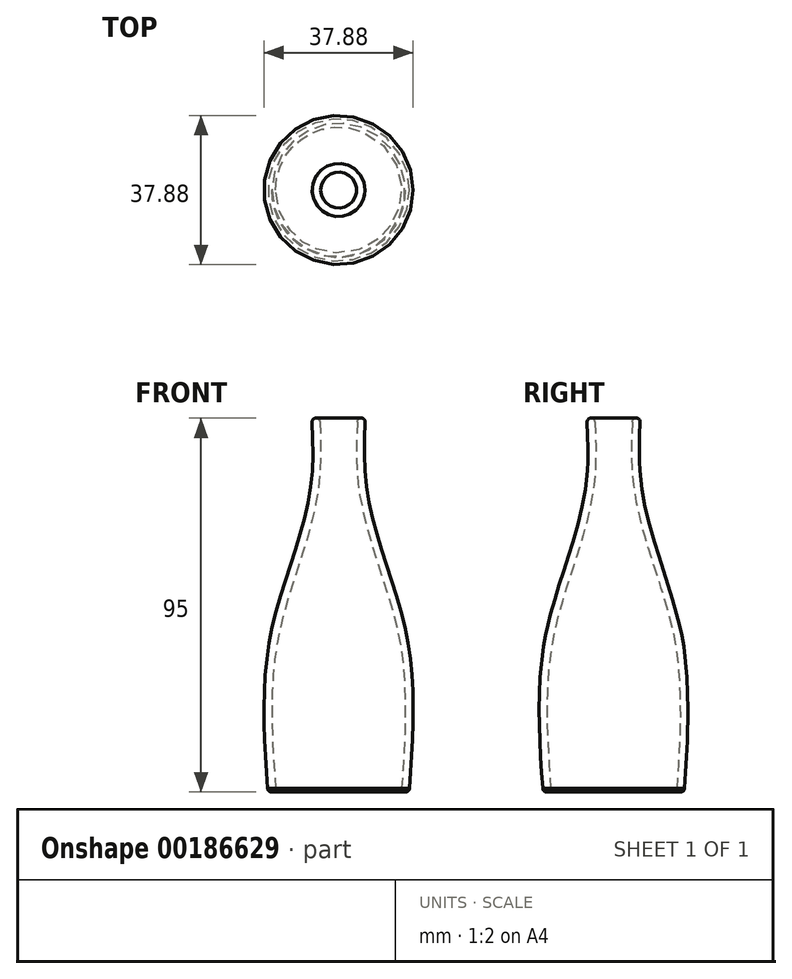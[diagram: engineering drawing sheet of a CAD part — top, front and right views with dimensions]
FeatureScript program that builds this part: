
annotation { "Feature Type Name" : "Feature", "Feature Type Description" : "" }
export const myFeature = defineFeature(function(context is Context, id is Id, definition is map)
    precondition{}
    {
        {
            var Q0;
            Q0=qCreatedBy(makeId("Top.planeOp"),FACE);
            var sketch = newSketch(context, id + "F0", { "sketchPlane" : qUnion([Q0])});
            skCircle(sketch, "E0", {"center": v(0, 0) * mm, "radius": 17.95 * mm});
            skPoint(sketch, "E1", {"position": v(0, 17.95) * mm});
            skPoint(sketch, "E2.1.0", {"position": v(-17.95, 0) * mm});
            skPoint(sketch, "E2.2.0", {"position": v(0, -17.95) * mm});
            skPoint(sketch, "E2.3.0", {"position": v(17.95, 0) * mm});
            skSolve(sketch);
        }
        {
            var Q0;
            Q0=qCreatedBy(makeId("Top.planeOp"),FACE);
            cPlane(context, id + "F1", {"entities" : qUnion([Q0]), "cplaneType" : CPlaneType.OFFSET, "offset" : 40 * mm, "width" : 150 * mm, "height" : 150 * mm});
        }
        {
            var Q0;
            Q0=qCreatedBy(id+"F1.planeOp",FACE);
            var sketch = newSketch(context, id + "F2", { "sketchPlane" : qUnion([Q0])});
            skCircle(sketch, "E3", {"center": v(0, 0) * mm, "radius": 17.25 * mm});
            skPoint(sketch, "E4", {"position": v(0, 17.25) * mm});
            skPoint(sketch, "E5.1.0", {"position": v(-17.25, 0) * mm});
            skPoint(sketch, "E5.2.0", {"position": v(0, -17.25) * mm});
            skPoint(sketch, "E5.3.0", {"position": v(17.25, 0) * mm});
            skSolve(sketch);
        }
        {
            var Q0;
            Q0=qCreatedBy(id+"F1.planeOp",FACE);
            cPlane(context, id + "F3", {"entities" : qUnion([Q0]), "cplaneType" : CPlaneType.OFFSET, "offset" : 40 * mm, "width" : 150 * mm, "height" : 150 * mm});
        }
        {
            var Q0;
            Q0=qCreatedBy(id+"F3.planeOp",FACE);
            var sketch = newSketch(context, id + "F4", { "sketchPlane" : qUnion([Q0])});
            skCircle(sketch, "E6", {"center": v(0, 0) * mm, "radius": 6.8 * mm});
            skSolve(sketch);
        }
        {
            var Q0;
            Q0=qCreatedBy(id+"F3.planeOp",FACE);
            cPlane(context, id + "F5", {"entities" : qUnion([Q0]), "cplaneType" : CPlaneType.OFFSET, "offset" : 15 * mm, "width" : 150 * mm, "height" : 150 * mm});
        }
        {
            var Q0;
            Q0=qCreatedBy(id+"F5.planeOp",FACE);
            var sketch = newSketch(context, id + "F6", { "sketchPlane" : qUnion([Q0])});
            skCircle(sketch, "E7", {"center": v(0, 0) * mm, "radius": 6.8 * mm});
            skSolve(sketch);
        }
        {
            var Q0;
            Q0=makeQuery(id+"F6.imprint","IMPRINT",FACE,{"disambiguationData":[TD([[makeQuery(id+"F6.imprint","IMPRINT",EDGE,{"derivedFrom":sQuery(id+"F6.wireOp",EDGE,"E7")}),1.0]])]});
            var Q1;
            Q1=makeQuery(id+"F4.imprint","IMPRINT",FACE,{"disambiguationData":[TD([[makeQuery(id+"F4.imprint","IMPRINT",EDGE,{"derivedFrom":sQuery(id+"F4.wireOp",EDGE,"E6")}),1.0]])]});
            var Q2;
            Q2=makeQuery(id+"F2.imprint","IMPRINT",FACE,{"disambiguationData":[TD([[makeQuery(id+"F2.imprint","IMPRINT",EDGE,{"derivedFrom":sQuery(id+"F2.wireOp",EDGE,"E3")}),1.0]])]});
            var Q3;
            Q3=makeQuery(id+"F0.imprint","IMPRINT",FACE,{"disambiguationData":[TD([[makeQuery(id+"F0.imprint","IMPRINT",EDGE,{"derivedFrom":sQuery(id+"F0.wireOp",EDGE,"E0")}),1.0]])]});
            loft(context, id + "F7", {"sheetProfilesArray" : [{ "sheetProfileEntities" : qUnion([Q0]) }, { "sheetProfileEntities" : qUnion([Q1]) }, { "sheetProfileEntities" : qUnion([Q2]) }, { "sheetProfileEntities" : qUnion([Q3]) }]});
        }
        {
            var Q0;
            Q0=makeQuery(id+"F7.opLoft","CAP_FACE",FACE,{"disambiguationData":[OSD([makeQuery(id+"F6.imprint","IMPRINT",FACE,{"disambiguationData":[TD([[makeQuery(id+"F6.imprint","IMPRINT",EDGE,{"derivedFrom":sQuery(id+"F6.wireOp",EDGE,"E7")}),1.0]])]})])],"isStart":true});
            var Q1;
            Q1=makeQuery(id+"F7.opLoft","CAP_FACE",FACE,{"disambiguationData":[OSD([makeQuery(id+"F0.imprint","IMPRINT",FACE,{"disambiguationData":[TD([[makeQuery(id+"F0.imprint","IMPRINT",EDGE,{"derivedFrom":sQuery(id+"F0.wireOp",EDGE,"E0")}),1.0]])]})])],"isStart":true});
            shell(context, id + "F8", {"entities" : qUnion([Q0, Q1]), "thickness" : 2 * mm});
        }
        {
            var Q0;
            Q0=makeQuery(id+"F8.opShell","OFFSET_EDGE",EDGE,{"disambiguationData":[OSD([sQuery(id+"F0.wireOp",EDGE,"E0")])]});
            var Q1;
            Q1=makeQuery(id+"F7.opLoft","MID_CAP_EDGE",EDGE,{"disambiguationData":[OSD([sQuery(id+"F0.wireOp",EDGE,"E0")])],"capPos":0.0});
            var Q2;
            Q2=makeQuery(id+"F8.opShell","OFFSET_EDGE",EDGE,{"disambiguationData":[OSD([sQuery(id+"F0.wireOp",EDGE,"E0"),sQuery(id+"F6.wireOp",EDGE,"E7")])]});
            var Q3;
            Q3=makeQuery(id+"F7.opLoft","MID_CAP_EDGE",EDGE,{"disambiguationData":[OSD([sQuery(id+"F0.wireOp",EDGE,"E0"),sQuery(id+"F6.wireOp",EDGE,"E7")])],"capPos":3.0});
            var Q4;
            Q4=makeQuery(id+"F8.opShell","OFFSET_EDGE",EDGE,{"disambiguationData":[OSD([sQuery(id+"F6.wireOp",EDGE,"E7")])]});
            var Q5;
            Q5=makeQuery(id+"F7.opLoft","MID_CAP_EDGE",EDGE,{"disambiguationData":[OSD([sQuery(id+"F6.wireOp",EDGE,"E7")])],"capPos":0.0});
            fillet(context, id + "F9", {"entities" : qUnion([Q0, Q1, Q2, Q3, Q4, Q5]), "radius" : 1 * mm, "tangentPropagation" : true, "allowEdgeOverflow" : false});
        }
    });
